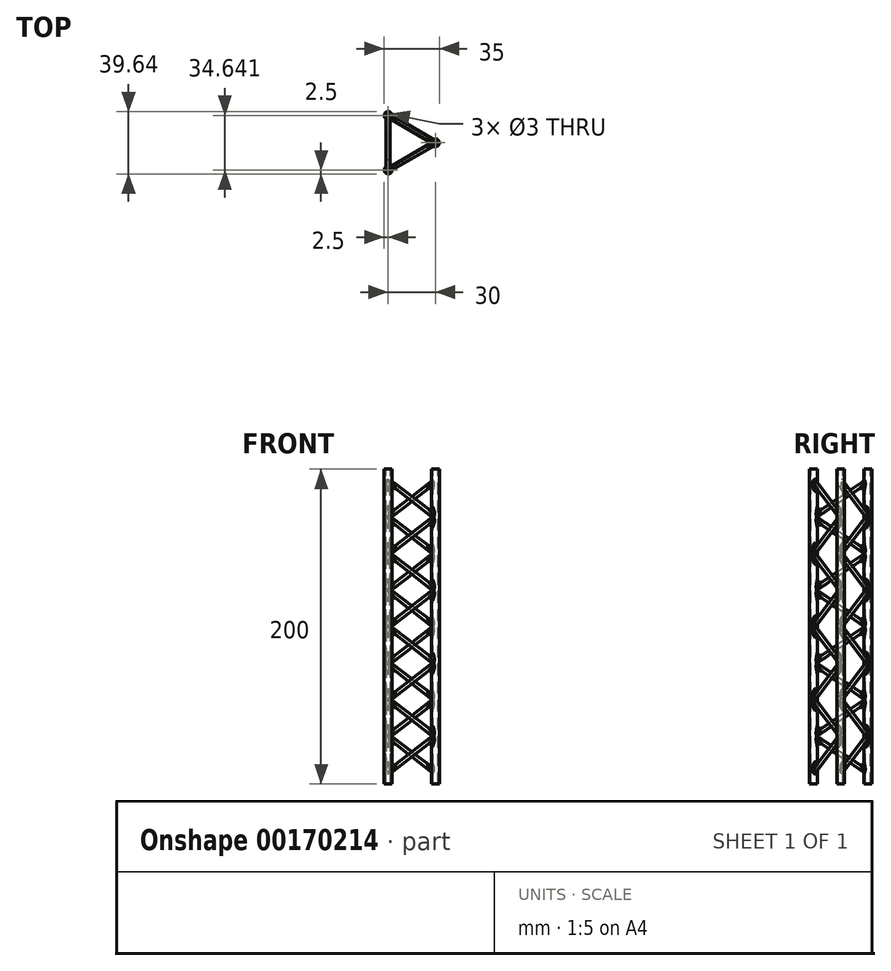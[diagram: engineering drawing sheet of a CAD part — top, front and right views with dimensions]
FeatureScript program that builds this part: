
annotation { "Feature Type Name" : "Feature", "Feature Type Description" : "" }
export const myFeature = defineFeature(function(context is Context, id is Id, definition is map)
    precondition{}
    {
        {
            var Q0;
            Q0=qCreatedBy(makeId("Top.planeOp"),FACE);
            var sketch = newSketch(context, id + "F0", { "sketchPlane" : qUnion([Q0])});
            skCircle(sketch, "E0", {"center": v(20, 0) * mm, "radius": 2.5 * mm});
            skCircle(sketch, "E1.1.0", {"center": v(-10, -17.32) * mm, "radius": 2.5 * mm});
            skCircle(sketch, "E1.2.0", {"center": v(-10, 17.32) * mm, "radius": 2.5 * mm});
            skPoint(sketch, "E1.center", {"position": v(0, 0) * mm});
            skLineSegment(sketch, "E1.anchor1", {"start": v(0, 0) * mm, "end": v(20, 0) * mm, "construction": true});
            skLineSegment(sketch, "E1.anchor2", {"start": v(0, 0) * mm, "end": v(-10, 17.32) * mm, "construction": true});
            skSolve(sketch);
        }
        {
            var Q0;
            Q0 = qSketchRegion(id + "F0", true);
            extrude(context, id + "F1", {"entities" : qUnion([Q0]), "endBound" : BoundingType.SYMMETRIC, "depth" : 200 * mm});
        }
        {
            var Q0;
            Q0=qCreatedBy(makeId("Front.planeOp"),FACE);
            var sketch = newSketch(context, id + "F2", { "sketchPlane" : qUnion([Q0])});
            skLineSegment(sketch, "E2", {"start": v(20, 0) * mm, "end": v(20, 100) * mm, "construction": true});
            skLineSegment(sketch, "E3", {"start": v(0, 0) * mm, "end": v(0, 97.6) * mm, "construction": true});
            skSolve(sketch);
        }
        {
            var Q0;
            Q0=sQuery(id+"F2.wireOp",VERTEX,"E2.end");
            var Q1;
            Q1=sQuery(id+"F2.wireOp",VERTEX,"E2.start");
            var Q2;
            Q2=sQuery(id+"F0.wireOp",VERTEX,"E1.2.0.center");
            cPlane(context, id + "F3", {"entities" : qUnion([Q0, Q1, Q2]), "cplaneType" : CPlaneType.THREE_POINT, "offset" : 25 * mm, "width" : 150 * mm, "height" : 150 * mm});
        }
        {
            var Q0;
            Q0=qCreatedBy(id+"F3.planeOp",FACE);
            var sketch = newSketch(context, id + "F4", { "sketchPlane" : qUnion([Q0])});
            skLineSegment(sketch, "E4", {"start": v(17.32, 0) * mm, "end": v(-17.32, 23.18) * mm});
            skLineSegment(sketch, "E5", {"start": v(17.32, 0) * mm, "end": v(17.32, 98.65) * mm, "construction": true});
            skLineSegment(sketch, "E6", {"start": v(-17.32, 23.18) * mm, "end": v(17.32, 46.37) * mm});
            skLineSegment(sketch, "E7", {"start": v(17.32, 46.37) * mm, "end": v(-17.32, 69.55) * mm});
            skLineSegment(sketch, "E8", {"start": v(-17.32, 69.55) * mm, "end": v(17.32, 92.73) * mm});
            skLineSegment(sketch, "E9", {"start": v(-17.32, 0) * mm, "end": v(-17.32, 100) * mm, "construction": true});
            skPoint(sketch, "E10.center", {"position": v(17.32, 0) * mm});
            skLineSegment(sketch, "E11", {"start": v(17.32, 0) * mm, "end": v(-17.32, 0) * mm, "construction": true});
            skSolve(sketch);
        }
        {
            var Q0;
            Q0=sQuery(id+"F4.wireOp",EDGE,"E4");
            var Q1;
            Q1=sQuery(id+"F4.wireOp",VERTEX,"E4.start");
            cPlane(context, id + "F5", {"entities" : qUnion([Q0, Q1]), "cplaneType" : CPlaneType.LINE_POINT, "offset" : 25 * mm, "width" : 150 * mm, "height" : 150 * mm});
        }
        {
            var Q0;
            Q0=qCreatedBy(id+"F5.planeOp",FACE);
            var sketch = newSketch(context, id + "F6", { "sketchPlane" : qUnion([Q0])});
            skCircle(sketch, "E12", {"center": v(-6.58, 12.23) * mm, "radius": 1.25 * mm});
            skSolve(sketch);
        }
        {
            var Q0;
            Q0 = qSketchRegion(id + "F6", true);
            var Q1;
            Q1 = qConstructionFilter(qBodyType(qCreatedBy(id + "F4" ,EDGE), BodyType.WIRE), ConstructionObject.NO);
            sweep(context, id + "F7", {"profiles" : qUnion([Q0]), "path" : qUnion([Q1])});
        }
        {
            var Q0;
            Q0=qCreatedBy(makeId("Top.planeOp"),FACE);
            var sketch = newSketch(context, id + "F8", { "sketchPlane" : qUnion([Q0])});
            skLineSegment(sketch, "E13", {"start": v(-10, 17.32) * mm, "end": v(20, 0) * mm});
            skSolve(sketch);
        }
        {
            var Q0;
            Q0=makeQuery(id+"F7.opSweep","SWEPT_BODY",BODY,{"disambiguationData":[OSD([sQuery(id+"F4.wireOp",EDGE,"E8"),sQuery(id+"F6.wireOp",EDGE,"E12")])]});
            var Q1;
            Q1=sQuery(id+"F8.wireOp",EDGE,"E13");
            circularPattern(context, id + "F9", {"entities" : qUnion([Q0]), "axis" : qUnion([Q1]), "angle" : 180 * degree, "instanceCount" : 2});
        }
        {
            var Q0;
            Q0=makeQuery(id+"F9.opPattern","COPY",BODY,{"derivedFrom":makeQuery(id+"F7.opSweep","SWEPT_BODY",BODY,{"disambiguationData":[OSD([sQuery(id+"F4.wireOp",EDGE,"E8"),sQuery(id+"F6.wireOp",EDGE,"E12")])]}),"instanceName":"1"});
            var Q1;
            Q1=makeQuery(id+"F7.opSweep","SWEPT_BODY",BODY,{"disambiguationData":[OSD([sQuery(id+"F4.wireOp",EDGE,"E8"),sQuery(id+"F6.wireOp",EDGE,"E12")])]});
            var Q2;
            Q2=sQuery(id+"F2.wireOp",EDGE,"E3");
            circularPattern(context, id + "F10", {"entities" : qUnion([Q0, Q1]), "axis" : qUnion([Q2]), "angle" : 120 * degree, "instanceCount" : 3});
        }
        {
            var Q0;
            Q0=makeQuery(id+"F1.opExtrude","SWEPT_BODY",BODY,{"disambiguationData":[OSD([sQuery(id+"F0.wireOp",EDGE,"E0")])]});
            var Q1;
            Q1=makeQuery(id+"F1.opExtrude","SWEPT_BODY",BODY,{"disambiguationData":[OSD([sQuery(id+"F0.wireOp",EDGE,"E1.1.0")])]});
            var Q2;
            Q2=makeQuery(id+"F7.opSweep","SWEPT_BODY",BODY,{"disambiguationData":[OSD([sQuery(id+"F4.wireOp",EDGE,"E8"),sQuery(id+"F6.wireOp",EDGE,"E12")])]});
            var Q3;
            Q3=makeQuery(id+"F9.opPattern","COPY",BODY,{"derivedFrom":makeQuery(id+"F7.opSweep","SWEPT_BODY",BODY,{"disambiguationData":[OSD([sQuery(id+"F4.wireOp",EDGE,"E8"),sQuery(id+"F6.wireOp",EDGE,"E12")])]}),"instanceName":"1"});
            var Q4;
            Q4=makeQuery(id+"F10.opPattern","COPY",BODY,{"derivedFrom":makeQuery(id+"F7.opSweep","SWEPT_BODY",BODY,{"disambiguationData":[OSD([sQuery(id+"F4.wireOp",EDGE,"E8"),sQuery(id+"F6.wireOp",EDGE,"E12")])]}),"instanceName":"2"});
            var Q5;
            Q5=makeQuery(id+"F10.opPattern","COPY",BODY,{"derivedFrom":makeQuery(id+"F9.opPattern","COPY",BODY,{"derivedFrom":makeQuery(id+"F7.opSweep","SWEPT_BODY",BODY,{"disambiguationData":[OSD([sQuery(id+"F4.wireOp",EDGE,"E8"),sQuery(id+"F6.wireOp",EDGE,"E12")])]}),"instanceName":"1"}),"instanceName":"2"});
            var Q6;
            Q6=makeQuery(id+"F1.opExtrude","SWEPT_BODY",BODY,{"disambiguationData":[OSD([sQuery(id+"F0.wireOp",EDGE,"E1.2.0")])]});
            var Q7;
            Q7=makeQuery(id+"F10.opPattern","COPY",BODY,{"derivedFrom":makeQuery(id+"F7.opSweep","SWEPT_BODY",BODY,{"disambiguationData":[OSD([sQuery(id+"F4.wireOp",EDGE,"E8"),sQuery(id+"F6.wireOp",EDGE,"E12")])]}),"instanceName":"1"});
            var Q8;
            Q8=makeQuery(id+"F10.opPattern","COPY",BODY,{"derivedFrom":makeQuery(id+"F9.opPattern","COPY",BODY,{"derivedFrom":makeQuery(id+"F7.opSweep","SWEPT_BODY",BODY,{"disambiguationData":[OSD([sQuery(id+"F4.wireOp",EDGE,"E8"),sQuery(id+"F6.wireOp",EDGE,"E12")])]}),"instanceName":"1"}),"instanceName":"1"});
            booleanBodies(context, id + "F11", {"operationType" : BooleanOperationType.UNION, "tools" : qUnion([Q0, Q1, Q2, Q3, Q4, Q5, Q6, Q7, Q8])});
        }
        {
            var Q0;
            Q0=makeQuery(id+"F11.opBoolean","INTERSECT",EDGE,{"derivedFrom":[makeQuery(id+"F1.opExtrude","SWEPT_FACE",FACE,{"disambiguationData":[OSD([sQuery(id+"F0.wireOp",EDGE,"E1.2.0")])]}),makeQuery(id+"F10.opPattern","COPY",FACE,{"derivedFrom":makeQuery(id+"F7.opSweep","SWEPT_FACE",FACE,{"disambiguationData":[OSD([sQuery(id+"F4.wireOp",EDGE,"E8"),sQuery(id+"F6.wireOp",EDGE,"E12")])]}),"instanceName":"1"})]});
            var Q1;
            Q1=makeQuery(id+"F11.opBoolean","INTERSECT",EDGE,{"derivedFrom":[makeQuery(id+"F1.opExtrude","SWEPT_FACE",FACE,{"disambiguationData":[OSD([sQuery(id+"F0.wireOp",EDGE,"E0")])]}),makeQuery(id+"F7.opSweep","SWEPT_FACE",FACE,{"disambiguationData":[OSD([sQuery(id+"F4.wireOp",EDGE,"E8"),sQuery(id+"F6.wireOp",EDGE,"E12")])]})]});
            var Q2;
            Q2=makeQuery(id+"F11.opBoolean","INTERSECT",EDGE,{"derivedFrom":[makeQuery(id+"F1.opExtrude","SWEPT_FACE",FACE,{"disambiguationData":[OSD([sQuery(id+"F0.wireOp",EDGE,"E0")])]}),makeQuery(id+"F10.opPattern","COPY",FACE,{"derivedFrom":makeQuery(id+"F7.opSweep","SWEPT_FACE",FACE,{"disambiguationData":[OSD([sQuery(id+"F4.wireOp",EDGE,"E8"),sQuery(id+"F6.wireOp",EDGE,"E12")])]}),"instanceName":"2"})]});
            var Q3;
            Q3=makeQuery(id+"F11.opBoolean","INTERSECT",EDGE,{"derivedFrom":[makeQuery(id+"F1.opExtrude","SWEPT_FACE",FACE,{"disambiguationData":[OSD([sQuery(id+"F0.wireOp",EDGE,"E0")])]}),makeQuery(id+"F10.opPattern","COPY",FACE,{"derivedFrom":makeQuery(id+"F7.opSweep","SWEPT_FACE",FACE,{"disambiguationData":[OSD([sQuery(id+"F4.wireOp",EDGE,"E7"),sQuery(id+"F6.wireOp",EDGE,"E12")])]}),"instanceName":"2"})]});
            var Q4;
            Q4=makeQuery(id+"F11.opBoolean","INTERSECT",EDGE,{"derivedFrom":[makeQuery(id+"F1.opExtrude","SWEPT_FACE",FACE,{"disambiguationData":[OSD([sQuery(id+"F0.wireOp",EDGE,"E0")])]}),makeQuery(id+"F7.opSweep","SWEPT_FACE",FACE,{"disambiguationData":[OSD([sQuery(id+"F4.wireOp",EDGE,"E7"),sQuery(id+"F6.wireOp",EDGE,"E12")])]})]});
            var Q5;
            Q5=makeQuery(id+"F11.opBoolean","INTERSECT",EDGE,{"derivedFrom":[makeQuery(id+"F1.opExtrude","SWEPT_FACE",FACE,{"disambiguationData":[OSD([sQuery(id+"F0.wireOp",EDGE,"E0")])]}),makeQuery(id+"F7.opSweep","SWEPT_FACE",FACE,{"disambiguationData":[OSD([sQuery(id+"F4.wireOp",EDGE,"E6"),sQuery(id+"F6.wireOp",EDGE,"E12")])]})]});
            var Q6;
            Q6=makeQuery(id+"F11.opBoolean","INTERSECT",EDGE,{"derivedFrom":[makeQuery(id+"F1.opExtrude","SWEPT_FACE",FACE,{"disambiguationData":[OSD([sQuery(id+"F0.wireOp",EDGE,"E0")])]}),makeQuery(id+"F10.opPattern","COPY",FACE,{"derivedFrom":makeQuery(id+"F7.opSweep","SWEPT_FACE",FACE,{"disambiguationData":[OSD([sQuery(id+"F4.wireOp",EDGE,"E6"),sQuery(id+"F6.wireOp",EDGE,"E12")])]}),"instanceName":"2"})]});
            var Q7;
            Q7=makeQuery(id+"F11.opBoolean","INTERSECT",EDGE,{"derivedFrom":[makeQuery(id+"F1.opExtrude","SWEPT_FACE",FACE,{"disambiguationData":[OSD([sQuery(id+"F0.wireOp",EDGE,"E0")])]}),makeQuery(id+"F10.opPattern","COPY",FACE,{"derivedFrom":makeQuery(id+"F7.opSweep","SWEPT_FACE",FACE,{"disambiguationData":[OSD([sQuery(id+"F4.wireOp",EDGE,"E4"),sQuery(id+"F6.wireOp",EDGE,"E12")])]}),"instanceName":"2"})]});
            var Q8;
            Q8=makeQuery(id+"F11.opBoolean","INTERSECT",EDGE,{"derivedFrom":[makeQuery(id+"F1.opExtrude","SWEPT_FACE",FACE,{"disambiguationData":[OSD([sQuery(id+"F0.wireOp",EDGE,"E0")])]}),makeQuery(id+"F7.opSweep","SWEPT_FACE",FACE,{"disambiguationData":[OSD([sQuery(id+"F4.wireOp",EDGE,"E4"),sQuery(id+"F6.wireOp",EDGE,"E12")])]})]});
            var Q9;
            Q9=makeQuery(id+"F11.opBoolean","INTERSECT",EDGE,{"derivedFrom":[makeQuery(id+"F1.opExtrude","SWEPT_FACE",FACE,{"disambiguationData":[OSD([sQuery(id+"F0.wireOp",EDGE,"E0")])]}),makeQuery(id+"F9.opPattern","COPY",FACE,{"derivedFrom":makeQuery(id+"F7.opSweep","SWEPT_FACE",FACE,{"disambiguationData":[OSD([sQuery(id+"F4.wireOp",EDGE,"E4"),sQuery(id+"F6.wireOp",EDGE,"E12")])]}),"instanceName":"1"})]});
            var Q10;
            Q10=makeQuery(id+"F11.opBoolean","INTERSECT",EDGE,{"derivedFrom":[makeQuery(id+"F1.opExtrude","SWEPT_FACE",FACE,{"disambiguationData":[OSD([sQuery(id+"F0.wireOp",EDGE,"E0")])]}),makeQuery(id+"F10.opPattern","COPY",FACE,{"derivedFrom":makeQuery(id+"F9.opPattern","COPY",FACE,{"derivedFrom":makeQuery(id+"F7.opSweep","SWEPT_FACE",FACE,{"disambiguationData":[OSD([sQuery(id+"F4.wireOp",EDGE,"E4"),sQuery(id+"F6.wireOp",EDGE,"E12")])]}),"instanceName":"1"}),"instanceName":"2"})]});
            var Q11;
            Q11=makeQuery(id+"F11.opBoolean","INTERSECT",EDGE,{"derivedFrom":[makeQuery(id+"F1.opExtrude","SWEPT_FACE",FACE,{"disambiguationData":[OSD([sQuery(id+"F0.wireOp",EDGE,"E0")])]}),makeQuery(id+"F10.opPattern","COPY",FACE,{"derivedFrom":makeQuery(id+"F9.opPattern","COPY",FACE,{"derivedFrom":makeQuery(id+"F7.opSweep","SWEPT_FACE",FACE,{"disambiguationData":[OSD([sQuery(id+"F4.wireOp",EDGE,"E6"),sQuery(id+"F6.wireOp",EDGE,"E12")])]}),"instanceName":"1"}),"instanceName":"2"})]});
            var Q12;
            Q12=makeQuery(id+"F11.opBoolean","INTERSECT",EDGE,{"derivedFrom":[makeQuery(id+"F1.opExtrude","SWEPT_FACE",FACE,{"disambiguationData":[OSD([sQuery(id+"F0.wireOp",EDGE,"E0")])]}),makeQuery(id+"F9.opPattern","COPY",FACE,{"derivedFrom":makeQuery(id+"F7.opSweep","SWEPT_FACE",FACE,{"disambiguationData":[OSD([sQuery(id+"F4.wireOp",EDGE,"E6"),sQuery(id+"F6.wireOp",EDGE,"E12")])]}),"instanceName":"1"})]});
            var Q13;
            Q13=makeQuery(id+"F11.opBoolean","INTERSECT",EDGE,{"derivedFrom":[makeQuery(id+"F1.opExtrude","SWEPT_FACE",FACE,{"disambiguationData":[OSD([sQuery(id+"F0.wireOp",EDGE,"E0")])]}),makeQuery(id+"F9.opPattern","COPY",FACE,{"derivedFrom":makeQuery(id+"F7.opSweep","SWEPT_FACE",FACE,{"disambiguationData":[OSD([sQuery(id+"F4.wireOp",EDGE,"E7"),sQuery(id+"F6.wireOp",EDGE,"E12")])]}),"instanceName":"1"})]});
            var Q14;
            Q14=makeQuery(id+"F11.opBoolean","INTERSECT",EDGE,{"derivedFrom":[makeQuery(id+"F1.opExtrude","SWEPT_FACE",FACE,{"disambiguationData":[OSD([sQuery(id+"F0.wireOp",EDGE,"E0")])]}),makeQuery(id+"F10.opPattern","COPY",FACE,{"derivedFrom":makeQuery(id+"F9.opPattern","COPY",FACE,{"derivedFrom":makeQuery(id+"F7.opSweep","SWEPT_FACE",FACE,{"disambiguationData":[OSD([sQuery(id+"F4.wireOp",EDGE,"E7"),sQuery(id+"F6.wireOp",EDGE,"E12")])]}),"instanceName":"1"}),"instanceName":"2"})]});
            var Q15;
            Q15=makeQuery(id+"F11.opBoolean","INTERSECT",EDGE,{"derivedFrom":[makeQuery(id+"F1.opExtrude","SWEPT_FACE",FACE,{"disambiguationData":[OSD([sQuery(id+"F0.wireOp",EDGE,"E0")])]}),makeQuery(id+"F10.opPattern","COPY",FACE,{"derivedFrom":makeQuery(id+"F9.opPattern","COPY",FACE,{"derivedFrom":makeQuery(id+"F7.opSweep","SWEPT_FACE",FACE,{"disambiguationData":[OSD([sQuery(id+"F4.wireOp",EDGE,"E8"),sQuery(id+"F6.wireOp",EDGE,"E12")])]}),"instanceName":"1"}),"instanceName":"2"})]});
            var Q16;
            Q16=makeQuery(id+"F11.opBoolean","INTERSECT",EDGE,{"derivedFrom":[makeQuery(id+"F1.opExtrude","SWEPT_FACE",FACE,{"disambiguationData":[OSD([sQuery(id+"F0.wireOp",EDGE,"E0")])]}),makeQuery(id+"F9.opPattern","COPY",FACE,{"derivedFrom":makeQuery(id+"F7.opSweep","SWEPT_FACE",FACE,{"disambiguationData":[OSD([sQuery(id+"F4.wireOp",EDGE,"E8"),sQuery(id+"F6.wireOp",EDGE,"E12")])]}),"instanceName":"1"})]});
            var Q17;
            Q17=makeQuery(id+"F11.opBoolean","INTERSECT",EDGE,{"derivedFrom":[makeQuery(id+"F1.opExtrude","SWEPT_FACE",FACE,{"disambiguationData":[OSD([sQuery(id+"F0.wireOp",EDGE,"E1.1.0")])]}),makeQuery(id+"F10.opPattern","COPY",FACE,{"derivedFrom":makeQuery(id+"F7.opSweep","SWEPT_FACE",FACE,{"disambiguationData":[OSD([sQuery(id+"F4.wireOp",EDGE,"E8"),sQuery(id+"F6.wireOp",EDGE,"E12")])]}),"instanceName":"2"})]});
            var Q18;
            Q18=makeQuery(id+"F11.opBoolean","INTERSECT",EDGE,{"derivedFrom":[makeQuery(id+"F1.opExtrude","SWEPT_FACE",FACE,{"disambiguationData":[OSD([sQuery(id+"F0.wireOp",EDGE,"E1.1.0")])]}),makeQuery(id+"F10.opPattern","COPY",FACE,{"derivedFrom":makeQuery(id+"F7.opSweep","SWEPT_FACE",FACE,{"disambiguationData":[OSD([sQuery(id+"F4.wireOp",EDGE,"E8"),sQuery(id+"F6.wireOp",EDGE,"E12")])]}),"instanceName":"1"})]});
            var Q19;
            Q19=makeQuery(id+"F11.opBoolean","INTERSECT",EDGE,{"derivedFrom":[makeQuery(id+"F1.opExtrude","SWEPT_FACE",FACE,{"disambiguationData":[OSD([sQuery(id+"F0.wireOp",EDGE,"E1.1.0")])]}),makeQuery(id+"F10.opPattern","COPY",FACE,{"derivedFrom":makeQuery(id+"F7.opSweep","SWEPT_FACE",FACE,{"disambiguationData":[OSD([sQuery(id+"F4.wireOp",EDGE,"E7"),sQuery(id+"F6.wireOp",EDGE,"E12")])]}),"instanceName":"1"})]});
            var Q20;
            Q20=makeQuery(id+"F11.opBoolean","INTERSECT",EDGE,{"derivedFrom":[makeQuery(id+"F1.opExtrude","SWEPT_FACE",FACE,{"disambiguationData":[OSD([sQuery(id+"F0.wireOp",EDGE,"E1.1.0")])]}),makeQuery(id+"F10.opPattern","COPY",FACE,{"derivedFrom":makeQuery(id+"F7.opSweep","SWEPT_FACE",FACE,{"disambiguationData":[OSD([sQuery(id+"F4.wireOp",EDGE,"E7"),sQuery(id+"F6.wireOp",EDGE,"E12")])]}),"instanceName":"2"})]});
            var Q21;
            Q21=makeQuery(id+"F11.opBoolean","INTERSECT",EDGE,{"derivedFrom":[makeQuery(id+"F1.opExtrude","SWEPT_FACE",FACE,{"disambiguationData":[OSD([sQuery(id+"F0.wireOp",EDGE,"E1.1.0")])]}),makeQuery(id+"F10.opPattern","COPY",FACE,{"derivedFrom":makeQuery(id+"F7.opSweep","SWEPT_FACE",FACE,{"disambiguationData":[OSD([sQuery(id+"F4.wireOp",EDGE,"E6"),sQuery(id+"F6.wireOp",EDGE,"E12")])]}),"instanceName":"2"})]});
            var Q22;
            Q22=makeQuery(id+"F11.opBoolean","INTERSECT",EDGE,{"derivedFrom":[makeQuery(id+"F1.opExtrude","SWEPT_FACE",FACE,{"disambiguationData":[OSD([sQuery(id+"F0.wireOp",EDGE,"E1.1.0")])]}),makeQuery(id+"F10.opPattern","COPY",FACE,{"derivedFrom":makeQuery(id+"F7.opSweep","SWEPT_FACE",FACE,{"disambiguationData":[OSD([sQuery(id+"F4.wireOp",EDGE,"E6"),sQuery(id+"F6.wireOp",EDGE,"E12")])]}),"instanceName":"1"})]});
            var Q23;
            Q23=makeQuery(id+"F11.opBoolean","INTERSECT",EDGE,{"derivedFrom":[makeQuery(id+"F1.opExtrude","SWEPT_FACE",FACE,{"disambiguationData":[OSD([sQuery(id+"F0.wireOp",EDGE,"E1.1.0")])]}),makeQuery(id+"F10.opPattern","COPY",FACE,{"derivedFrom":makeQuery(id+"F7.opSweep","SWEPT_FACE",FACE,{"disambiguationData":[OSD([sQuery(id+"F4.wireOp",EDGE,"E4"),sQuery(id+"F6.wireOp",EDGE,"E12")])]}),"instanceName":"1"})]});
            var Q24;
            Q24=makeQuery(id+"F11.opBoolean","INTERSECT",EDGE,{"derivedFrom":[makeQuery(id+"F1.opExtrude","SWEPT_FACE",FACE,{"disambiguationData":[OSD([sQuery(id+"F0.wireOp",EDGE,"E1.1.0")])]}),makeQuery(id+"F10.opPattern","COPY",FACE,{"derivedFrom":makeQuery(id+"F7.opSweep","SWEPT_FACE",FACE,{"disambiguationData":[OSD([sQuery(id+"F4.wireOp",EDGE,"E4"),sQuery(id+"F6.wireOp",EDGE,"E12")])]}),"instanceName":"2"})]});
            var Q25;
            Q25=makeQuery(id+"F11.opBoolean","INTERSECT",EDGE,{"derivedFrom":[makeQuery(id+"F1.opExtrude","SWEPT_FACE",FACE,{"disambiguationData":[OSD([sQuery(id+"F0.wireOp",EDGE,"E1.1.0")])]}),makeQuery(id+"F10.opPattern","COPY",FACE,{"derivedFrom":makeQuery(id+"F9.opPattern","COPY",FACE,{"derivedFrom":makeQuery(id+"F7.opSweep","SWEPT_FACE",FACE,{"disambiguationData":[OSD([sQuery(id+"F4.wireOp",EDGE,"E4"),sQuery(id+"F6.wireOp",EDGE,"E12")])]}),"instanceName":"1"}),"instanceName":"2"})]});
            var Q26;
            Q26=makeQuery(id+"F11.opBoolean","INTERSECT",EDGE,{"derivedFrom":[makeQuery(id+"F1.opExtrude","SWEPT_FACE",FACE,{"disambiguationData":[OSD([sQuery(id+"F0.wireOp",EDGE,"E1.1.0")])]}),makeQuery(id+"F10.opPattern","COPY",FACE,{"derivedFrom":makeQuery(id+"F9.opPattern","COPY",FACE,{"derivedFrom":makeQuery(id+"F7.opSweep","SWEPT_FACE",FACE,{"disambiguationData":[OSD([sQuery(id+"F4.wireOp",EDGE,"E4"),sQuery(id+"F6.wireOp",EDGE,"E12")])]}),"instanceName":"1"}),"instanceName":"1"})]});
            var Q27;
            Q27=makeQuery(id+"F11.opBoolean","INTERSECT",EDGE,{"derivedFrom":[makeQuery(id+"F1.opExtrude","SWEPT_FACE",FACE,{"disambiguationData":[OSD([sQuery(id+"F0.wireOp",EDGE,"E1.1.0")])]}),makeQuery(id+"F10.opPattern","COPY",FACE,{"derivedFrom":makeQuery(id+"F9.opPattern","COPY",FACE,{"derivedFrom":makeQuery(id+"F7.opSweep","SWEPT_FACE",FACE,{"disambiguationData":[OSD([sQuery(id+"F4.wireOp",EDGE,"E6"),sQuery(id+"F6.wireOp",EDGE,"E12")])]}),"instanceName":"1"}),"instanceName":"1"})]});
            var Q28;
            Q28=makeQuery(id+"F11.opBoolean","INTERSECT",EDGE,{"derivedFrom":[makeQuery(id+"F1.opExtrude","SWEPT_FACE",FACE,{"disambiguationData":[OSD([sQuery(id+"F0.wireOp",EDGE,"E1.1.0")])]}),makeQuery(id+"F10.opPattern","COPY",FACE,{"derivedFrom":makeQuery(id+"F9.opPattern","COPY",FACE,{"derivedFrom":makeQuery(id+"F7.opSweep","SWEPT_FACE",FACE,{"disambiguationData":[OSD([sQuery(id+"F4.wireOp",EDGE,"E6"),sQuery(id+"F6.wireOp",EDGE,"E12")])]}),"instanceName":"1"}),"instanceName":"2"})]});
            var Q29;
            Q29=makeQuery(id+"F11.opBoolean","INTERSECT",EDGE,{"derivedFrom":[makeQuery(id+"F1.opExtrude","SWEPT_FACE",FACE,{"disambiguationData":[OSD([sQuery(id+"F0.wireOp",EDGE,"E1.1.0")])]}),makeQuery(id+"F10.opPattern","COPY",FACE,{"derivedFrom":makeQuery(id+"F9.opPattern","COPY",FACE,{"derivedFrom":makeQuery(id+"F7.opSweep","SWEPT_FACE",FACE,{"disambiguationData":[OSD([sQuery(id+"F4.wireOp",EDGE,"E7"),sQuery(id+"F6.wireOp",EDGE,"E12")])]}),"instanceName":"1"}),"instanceName":"2"})]});
            var Q30;
            Q30=makeQuery(id+"F11.opBoolean","INTERSECT",EDGE,{"derivedFrom":[makeQuery(id+"F1.opExtrude","SWEPT_FACE",FACE,{"disambiguationData":[OSD([sQuery(id+"F0.wireOp",EDGE,"E1.1.0")])]}),makeQuery(id+"F10.opPattern","COPY",FACE,{"derivedFrom":makeQuery(id+"F9.opPattern","COPY",FACE,{"derivedFrom":makeQuery(id+"F7.opSweep","SWEPT_FACE",FACE,{"disambiguationData":[OSD([sQuery(id+"F4.wireOp",EDGE,"E7"),sQuery(id+"F6.wireOp",EDGE,"E12")])]}),"instanceName":"1"}),"instanceName":"1"})]});
            var Q31;
            Q31=makeQuery(id+"F11.opBoolean","INTERSECT",EDGE,{"derivedFrom":[makeQuery(id+"F1.opExtrude","SWEPT_FACE",FACE,{"disambiguationData":[OSD([sQuery(id+"F0.wireOp",EDGE,"E1.1.0")])]}),makeQuery(id+"F10.opPattern","COPY",FACE,{"derivedFrom":makeQuery(id+"F9.opPattern","COPY",FACE,{"derivedFrom":makeQuery(id+"F7.opSweep","SWEPT_FACE",FACE,{"disambiguationData":[OSD([sQuery(id+"F4.wireOp",EDGE,"E8"),sQuery(id+"F6.wireOp",EDGE,"E12")])]}),"instanceName":"1"}),"instanceName":"1"})]});
            var Q32;
            Q32=makeQuery(id+"F11.opBoolean","INTERSECT",EDGE,{"derivedFrom":[makeQuery(id+"F1.opExtrude","SWEPT_FACE",FACE,{"disambiguationData":[OSD([sQuery(id+"F0.wireOp",EDGE,"E1.1.0")])]}),makeQuery(id+"F10.opPattern","COPY",FACE,{"derivedFrom":makeQuery(id+"F9.opPattern","COPY",FACE,{"derivedFrom":makeQuery(id+"F7.opSweep","SWEPT_FACE",FACE,{"disambiguationData":[OSD([sQuery(id+"F4.wireOp",EDGE,"E8"),sQuery(id+"F6.wireOp",EDGE,"E12")])]}),"instanceName":"1"}),"instanceName":"2"})]});
            var Q33;
            Q33=makeQuery(id+"F11.opBoolean","INTERSECT",EDGE,{"derivedFrom":[makeQuery(id+"F1.opExtrude","SWEPT_FACE",FACE,{"disambiguationData":[OSD([sQuery(id+"F0.wireOp",EDGE,"E1.2.0")])]}),makeQuery(id+"F10.opPattern","COPY",FACE,{"derivedFrom":makeQuery(id+"F9.opPattern","COPY",FACE,{"derivedFrom":makeQuery(id+"F7.opSweep","SWEPT_FACE",FACE,{"disambiguationData":[OSD([sQuery(id+"F4.wireOp",EDGE,"E8"),sQuery(id+"F6.wireOp",EDGE,"E12")])]}),"instanceName":"1"}),"instanceName":"1"})]});
            var Q34;
            Q34=makeQuery(id+"F11.opBoolean","INTERSECT",EDGE,{"derivedFrom":[makeQuery(id+"F1.opExtrude","SWEPT_FACE",FACE,{"disambiguationData":[OSD([sQuery(id+"F0.wireOp",EDGE,"E1.2.0")])]}),makeQuery(id+"F9.opPattern","COPY",FACE,{"derivedFrom":makeQuery(id+"F7.opSweep","SWEPT_FACE",FACE,{"disambiguationData":[OSD([sQuery(id+"F4.wireOp",EDGE,"E8"),sQuery(id+"F6.wireOp",EDGE,"E12")])]}),"instanceName":"1"})]});
            var Q35;
            Q35=makeQuery(id+"F11.opBoolean","INTERSECT",EDGE,{"derivedFrom":[makeQuery(id+"F1.opExtrude","SWEPT_FACE",FACE,{"disambiguationData":[OSD([sQuery(id+"F0.wireOp",EDGE,"E1.2.0")])]}),makeQuery(id+"F9.opPattern","COPY",FACE,{"derivedFrom":makeQuery(id+"F7.opSweep","SWEPT_FACE",FACE,{"disambiguationData":[OSD([sQuery(id+"F4.wireOp",EDGE,"E7"),sQuery(id+"F6.wireOp",EDGE,"E12")])]}),"instanceName":"1"})]});
            var Q36;
            Q36=makeQuery(id+"F11.opBoolean","INTERSECT",EDGE,{"derivedFrom":[makeQuery(id+"F1.opExtrude","SWEPT_FACE",FACE,{"disambiguationData":[OSD([sQuery(id+"F0.wireOp",EDGE,"E1.2.0")])]}),makeQuery(id+"F10.opPattern","COPY",FACE,{"derivedFrom":makeQuery(id+"F9.opPattern","COPY",FACE,{"derivedFrom":makeQuery(id+"F7.opSweep","SWEPT_FACE",FACE,{"disambiguationData":[OSD([sQuery(id+"F4.wireOp",EDGE,"E6"),sQuery(id+"F6.wireOp",EDGE,"E12")])]}),"instanceName":"1"}),"instanceName":"1"})]});
            var Q37;
            Q37=makeQuery(id+"F11.opBoolean","INTERSECT",EDGE,{"derivedFrom":[makeQuery(id+"F1.opExtrude","SWEPT_FACE",FACE,{"disambiguationData":[OSD([sQuery(id+"F0.wireOp",EDGE,"E1.2.0")])]}),makeQuery(id+"F10.opPattern","COPY",FACE,{"derivedFrom":makeQuery(id+"F9.opPattern","COPY",FACE,{"derivedFrom":makeQuery(id+"F7.opSweep","SWEPT_FACE",FACE,{"disambiguationData":[OSD([sQuery(id+"F4.wireOp",EDGE,"E7"),sQuery(id+"F6.wireOp",EDGE,"E12")])]}),"instanceName":"1"}),"instanceName":"1"})]});
            var Q38;
            Q38=makeQuery(id+"F11.opBoolean","INTERSECT",EDGE,{"derivedFrom":[makeQuery(id+"F1.opExtrude","SWEPT_FACE",FACE,{"disambiguationData":[OSD([sQuery(id+"F0.wireOp",EDGE,"E1.2.0")])]}),makeQuery(id+"F9.opPattern","COPY",FACE,{"derivedFrom":makeQuery(id+"F7.opSweep","SWEPT_FACE",FACE,{"disambiguationData":[OSD([sQuery(id+"F4.wireOp",EDGE,"E6"),sQuery(id+"F6.wireOp",EDGE,"E12")])]}),"instanceName":"1"})]});
            var Q39;
            Q39=makeQuery(id+"F11.opBoolean","INTERSECT",EDGE,{"derivedFrom":[makeQuery(id+"F1.opExtrude","SWEPT_FACE",FACE,{"disambiguationData":[OSD([sQuery(id+"F0.wireOp",EDGE,"E1.2.0")])]}),makeQuery(id+"F9.opPattern","COPY",FACE,{"derivedFrom":makeQuery(id+"F7.opSweep","SWEPT_FACE",FACE,{"disambiguationData":[OSD([sQuery(id+"F4.wireOp",EDGE,"E4"),sQuery(id+"F6.wireOp",EDGE,"E12")])]}),"instanceName":"1"})]});
            var Q40;
            Q40=makeQuery(id+"F11.opBoolean","INTERSECT",EDGE,{"derivedFrom":[makeQuery(id+"F1.opExtrude","SWEPT_FACE",FACE,{"disambiguationData":[OSD([sQuery(id+"F0.wireOp",EDGE,"E1.2.0")])]}),makeQuery(id+"F10.opPattern","COPY",FACE,{"derivedFrom":makeQuery(id+"F9.opPattern","COPY",FACE,{"derivedFrom":makeQuery(id+"F7.opSweep","SWEPT_FACE",FACE,{"disambiguationData":[OSD([sQuery(id+"F4.wireOp",EDGE,"E4"),sQuery(id+"F6.wireOp",EDGE,"E12")])]}),"instanceName":"1"}),"instanceName":"1"})]});
            var Q41;
            Q41=makeQuery(id+"F11.opBoolean","INTERSECT",EDGE,{"derivedFrom":[makeQuery(id+"F1.opExtrude","SWEPT_FACE",FACE,{"disambiguationData":[OSD([sQuery(id+"F0.wireOp",EDGE,"E1.2.0")])]}),makeQuery(id+"F10.opPattern","COPY",FACE,{"derivedFrom":makeQuery(id+"F7.opSweep","SWEPT_FACE",FACE,{"disambiguationData":[OSD([sQuery(id+"F4.wireOp",EDGE,"E4"),sQuery(id+"F6.wireOp",EDGE,"E12")])]}),"instanceName":"1"})]});
            var Q42;
            Q42=makeQuery(id+"F11.opBoolean","INTERSECT",EDGE,{"derivedFrom":[makeQuery(id+"F1.opExtrude","SWEPT_FACE",FACE,{"disambiguationData":[OSD([sQuery(id+"F0.wireOp",EDGE,"E1.2.0")])]}),makeQuery(id+"F7.opSweep","SWEPT_FACE",FACE,{"disambiguationData":[OSD([sQuery(id+"F4.wireOp",EDGE,"E4"),sQuery(id+"F6.wireOp",EDGE,"E12")])]})]});
            var Q43;
            Q43=makeQuery(id+"F11.opBoolean","INTERSECT",EDGE,{"derivedFrom":[makeQuery(id+"F1.opExtrude","SWEPT_FACE",FACE,{"disambiguationData":[OSD([sQuery(id+"F0.wireOp",EDGE,"E1.2.0")])]}),makeQuery(id+"F7.opSweep","SWEPT_FACE",FACE,{"disambiguationData":[OSD([sQuery(id+"F4.wireOp",EDGE,"E6"),sQuery(id+"F6.wireOp",EDGE,"E12")])]})]});
            var Q44;
            Q44=makeQuery(id+"F11.opBoolean","INTERSECT",EDGE,{"derivedFrom":[makeQuery(id+"F1.opExtrude","SWEPT_FACE",FACE,{"disambiguationData":[OSD([sQuery(id+"F0.wireOp",EDGE,"E1.2.0")])]}),makeQuery(id+"F10.opPattern","COPY",FACE,{"derivedFrom":makeQuery(id+"F7.opSweep","SWEPT_FACE",FACE,{"disambiguationData":[OSD([sQuery(id+"F4.wireOp",EDGE,"E7"),sQuery(id+"F6.wireOp",EDGE,"E12")])]}),"instanceName":"1"})]});
            var Q45;
            Q45=makeQuery(id+"F11.opBoolean","INTERSECT",EDGE,{"derivedFrom":[makeQuery(id+"F1.opExtrude","SWEPT_FACE",FACE,{"disambiguationData":[OSD([sQuery(id+"F0.wireOp",EDGE,"E1.2.0")])]}),makeQuery(id+"F10.opPattern","COPY",FACE,{"derivedFrom":makeQuery(id+"F7.opSweep","SWEPT_FACE",FACE,{"disambiguationData":[OSD([sQuery(id+"F4.wireOp",EDGE,"E6"),sQuery(id+"F6.wireOp",EDGE,"E12")])]}),"instanceName":"1"})]});
            var Q46;
            Q46=makeQuery(id+"F11.opBoolean","INTERSECT",EDGE,{"derivedFrom":[makeQuery(id+"F1.opExtrude","SWEPT_FACE",FACE,{"disambiguationData":[OSD([sQuery(id+"F0.wireOp",EDGE,"E1.2.0")])]}),makeQuery(id+"F7.opSweep","SWEPT_FACE",FACE,{"disambiguationData":[OSD([sQuery(id+"F4.wireOp",EDGE,"E7"),sQuery(id+"F6.wireOp",EDGE,"E12")])]})]});
            var Q47;
            Q47=makeQuery(id+"F11.opBoolean","INTERSECT",EDGE,{"derivedFrom":[makeQuery(id+"F1.opExtrude","SWEPT_FACE",FACE,{"disambiguationData":[OSD([sQuery(id+"F0.wireOp",EDGE,"E1.2.0")])]}),makeQuery(id+"F7.opSweep","SWEPT_FACE",FACE,{"disambiguationData":[OSD([sQuery(id+"F4.wireOp",EDGE,"E8"),sQuery(id+"F6.wireOp",EDGE,"E12")])]})]});
            fillet(context, id + "F12", {"entities" : qUnion([Q0, Q1, Q2, Q3, Q4, Q5, Q6, Q7, Q8, Q9, Q10, Q11, Q12, Q13, Q14, Q15, Q16, Q17, Q18, Q19, Q20, Q21, Q22, Q23, Q24, Q25, Q26, Q27, Q28, Q29, Q30, Q31, Q32, Q33, Q34, Q35, Q36, Q37, Q38, Q39, Q40, Q41, Q42, Q43, Q44, Q45, Q46, Q47]), "radius" : 2 * mm, "tangentPropagation" : true, "allowEdgeOverflow" : false});
        }
        {
            var Q0;
            Q0=qCreatedBy(makeId("Top.planeOp"),FACE);
            var sketch = newSketch(context, id + "F13", { "sketchPlane" : qUnion([Q0])});
            skCircle(sketch, "E14", {"center": v(20, 0) * mm, "radius": 1.5 * mm});
            skCircle(sketch, "E15.1.0", {"center": v(-10, 17.32) * mm, "radius": 1.5 * mm});
            skCircle(sketch, "E15.2.0", {"center": v(-10, -17.32) * mm, "radius": 1.5 * mm});
            skPoint(sketch, "E15.center", {"position": v(0, 0) * mm});
            skSolve(sketch);
        }
        {
            var Q0;
            Q0 = qSketchRegion(id + "F13", true);
            extrude(context, id + "F14", {"entities" : qUnion([Q0]), "operationType" : NewBodyOperationType.REMOVE, "endBound" : BoundingType.SYMMETRIC, "oppositeDirection" : true, "depth" : 200 * mm});
        }
    });
